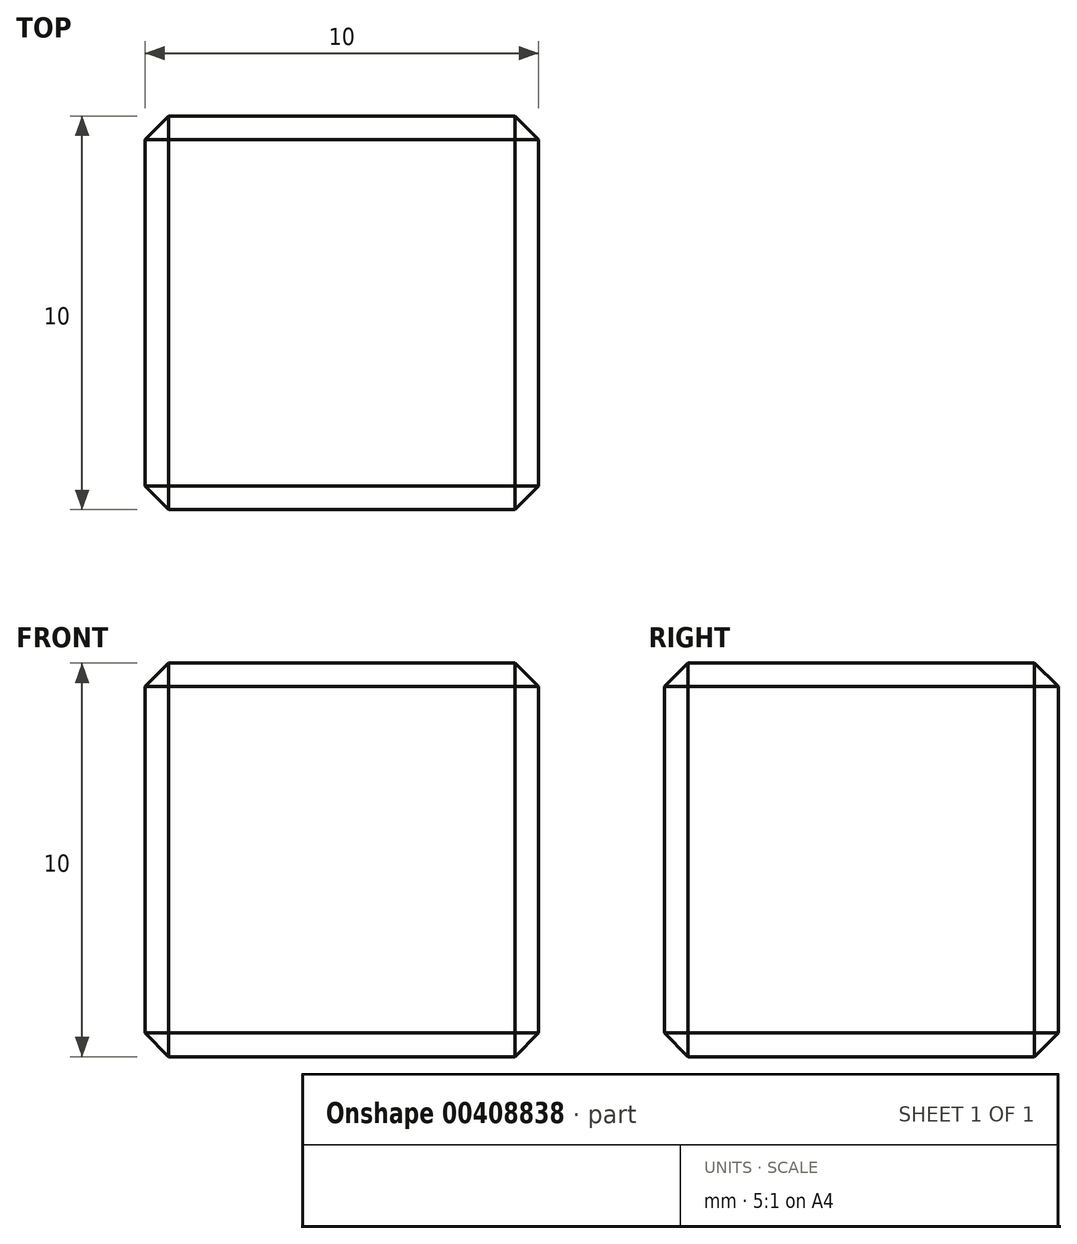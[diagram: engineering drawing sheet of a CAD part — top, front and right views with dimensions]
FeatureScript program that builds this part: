
annotation { "Feature Type Name" : "Feature", "Feature Type Description" : "" }
export const myFeature = defineFeature(function(context is Context, id is Id, definition is map)
    precondition{}
    {
        {
            var Q0;
            Q0=qCreatedBy(makeId("Top.planeOp"),FACE);
            var sketch = newSketch(context, id + "F0", { "sketchPlane" : qUnion([Q0])});
            skLineSegment(sketch, "E0.bottom", {"start": v(0, 0) * mm, "end": v(10, 0) * mm});
            skLineSegment(sketch, "E0.top", {"start": v(0, 10) * mm, "end": v(10, 10) * mm});
            skLineSegment(sketch, "E0.left", {"start": v(0, 0) * mm, "end": v(0, 10) * mm});
            skLineSegment(sketch, "E0.right", {"start": v(10, 0) * mm, "end": v(10, 10) * mm});
            skSolve(sketch);
        }
        {
            var Q0;
            Q0 = qSketchRegion(id + "F0", true);
            extrude(context, id + "F1", {"entities" : qUnion([Q0]), "depth" : 10 * mm});
        }
        {
            var Q0;
            Q0=makeQuery(id+"F1.opExtrude","CAP_FACE",FACE,{"disambiguationData":[OSD([sQuery(id+"F0.wireOp",EDGE,"E0.bottom"),sQuery(id+"F0.wireOp",EDGE,"E0.top"),sQuery(id+"F0.wireOp",EDGE,"E0.left"),sQuery(id+"F0.wireOp",EDGE,"E0.right")])],"isStart":true});
            var Q1;
            Q1=makeQuery(id+"F1.opExtrude","SWEPT_FACE",FACE,{"disambiguationData":[OSD([sQuery(id+"F0.wireOp",EDGE,"E0.left")])]});
            var Q2;
            Q2=makeQuery(id+"F1.opExtrude","CAP_FACE",FACE,{"disambiguationData":[OSD([sQuery(id+"F0.wireOp",EDGE,"E0.bottom"),sQuery(id+"F0.wireOp",EDGE,"E0.top"),sQuery(id+"F0.wireOp",EDGE,"E0.left"),sQuery(id+"F0.wireOp",EDGE,"E0.right")])],"isStart":false});
            var Q3;
            Q3=makeQuery(id+"F1.opExtrude","SWEPT_FACE",FACE,{"disambiguationData":[OSD([sQuery(id+"F0.wireOp",EDGE,"E0.right")])]});
            chamfer(context, id + "F2", {"entities" : qUnion([Q0, Q1, Q2, Q3]), "width" : 0.6 * mm, "tangentPropagation" : true});
        }
    });
